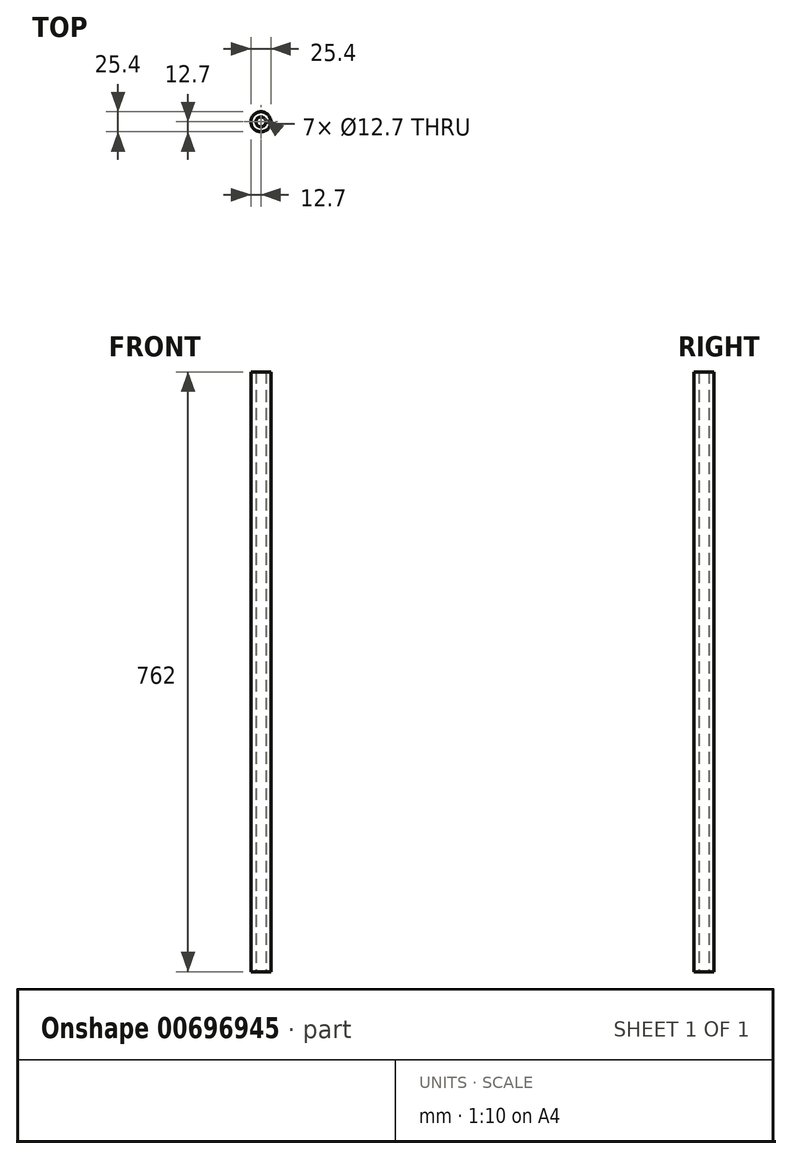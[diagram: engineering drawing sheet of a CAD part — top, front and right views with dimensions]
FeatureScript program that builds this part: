
annotation { "Feature Type Name" : "Feature", "Feature Type Description" : "" }
export const myFeature = defineFeature(function(context is Context, id is Id, definition is map)
    precondition{}
    {
        {
            var Q0;
            Q0=qCreatedBy(makeId("Top.planeOp"),FACE);
            var sketch = newSketch(context, id + "F0", { "sketchPlane" : qUnion([Q0])});
            skCircle(sketch, "E0", {"center": v(0, 0) * mm, "radius": 6.35 * mm});
            skCircle(sketch, "E1", {"center": v(0, 0) * mm, "radius": 12.7 * mm});
            skSolve(sketch);
        }
        {
            var Q0;
            Q0 = qSketchRegion(id + "F0", true);
            extrude(context, id + "F1", {"entities" : qUnion([Q0]), "depth" : 762 * mm, "offsetDistance" : 25.4 * mm});
        }
    });
